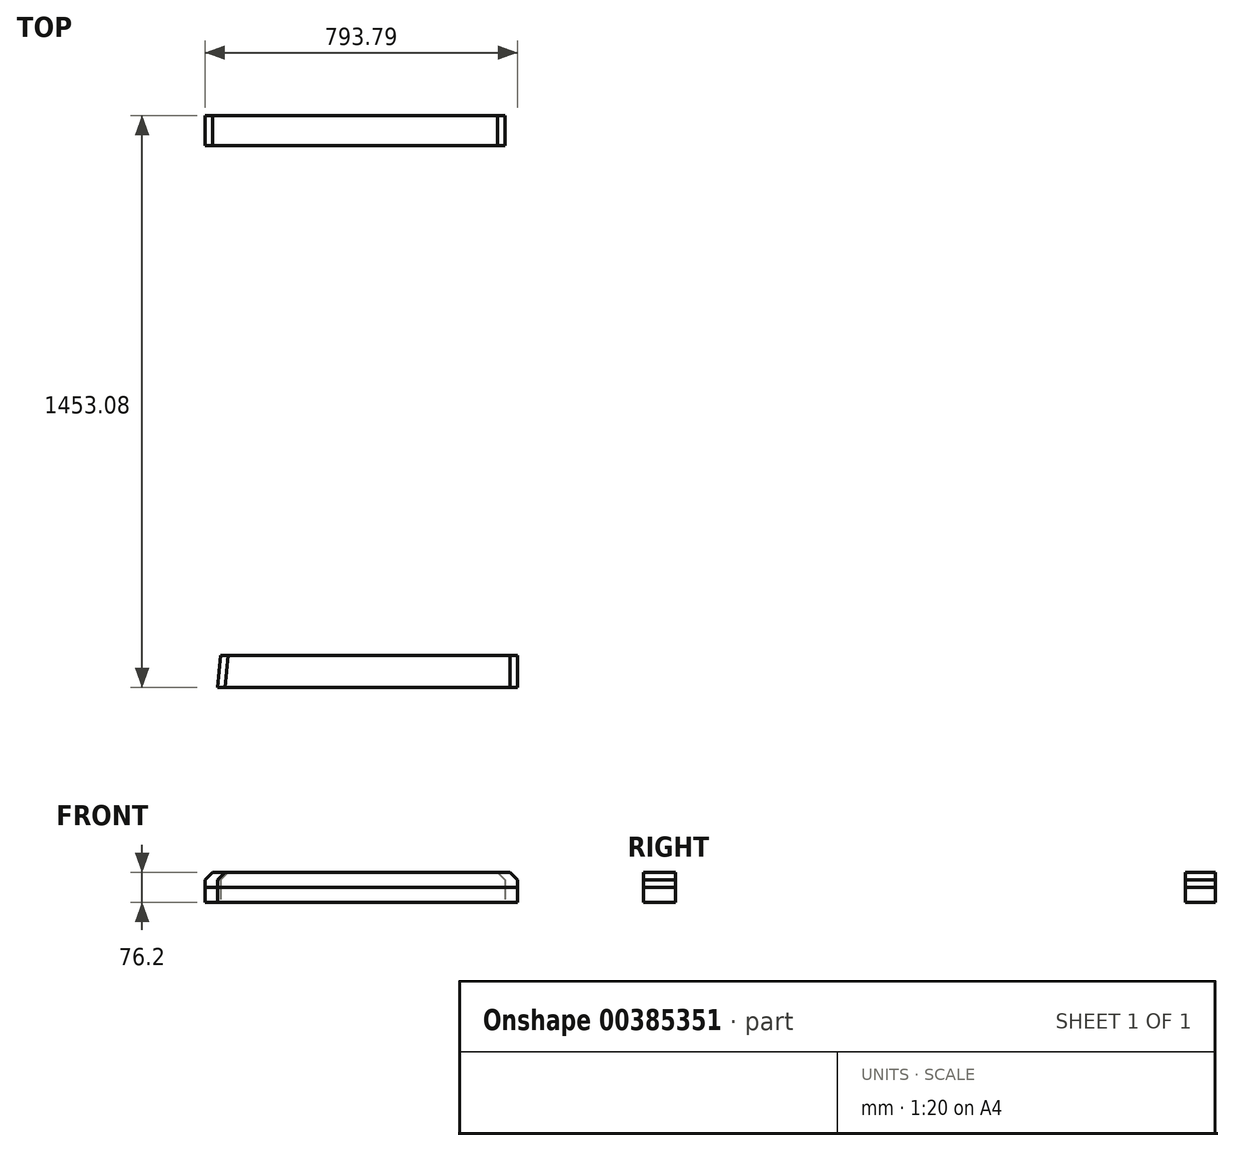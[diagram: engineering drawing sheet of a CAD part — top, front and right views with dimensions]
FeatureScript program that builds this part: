
annotation { "Feature Type Name" : "Feature", "Feature Type Description" : "" }
export const myFeature = defineFeature(function(context is Context, id is Id, definition is map)
    precondition{}
    {
        {
            var Q0;
            Q0=qCreatedBy(makeId("Top.planeOp"),FACE);
            var sketch = newSketch(context, id + "F0", { "sketchPlane" : qUnion([Q0])});
            skLineSegment(sketch, "E0", {"start": v(241.05, 8) * mm, "end": v(241.05, 84.2) * mm});
            skLineSegment(sketch, "E1", {"start": v(241.05, 84.2) * mm, "end": v(1003.05, 84.2) * mm});
            skLineSegment(sketch, "E2", {"start": v(1003.05, 84.2) * mm, "end": v(1003.05, 8) * mm});
            skLineSegment(sketch, "E3", {"start": v(1003.05, 8) * mm, "end": v(241.05, 8) * mm});
            skSolve(sketch);
        }
        {
            var Q0;
            Q0=qCreatedBy(makeId("Top.planeOp"),FACE);
            var sketch = newSketch(context, id + "F1", { "sketchPlane" : qUnion([Q0])});
            skLineSegment(sketch, "E4", {"start": v(280.2, -1287.3) * mm, "end": v(1034.84, -1287.3) * mm});
            skLineSegment(sketch, "E5", {"start": v(1034.84, -1287.3) * mm, "end": v(1034.84, -1368.88) * mm});
            skLineSegment(sketch, "E6", {"start": v(1034.84, -1368.88) * mm, "end": v(272.84, -1368.88) * mm});
            skLineSegment(sketch, "E7", {"start": v(272.84, -1368.88) * mm, "end": v(280.2, -1287.3) * mm});
            skSolve(sketch);
        }
        {
            var Q0;
            Q0=makeQuery(id+"F0.imprint","IMPRINT",FACE,{"disambiguationData":[TD([[makeQuery(id+"F0.imprint","IMPRINT",EDGE,{"derivedFrom":sQuery(id+"F0.wireOp",EDGE,"E0")}),-1.0]])]});
            extrude(context, id + "F2", {"entities" : qUnion([Q0]), "depth" : 38.1 * mm});
        }
        {
            var Q0;
            Q0=makeQuery(id+"F1.imprint","IMPRINT",FACE,{"disambiguationData":[TD([[makeQuery(id+"F1.imprint","IMPRINT",EDGE,{"derivedFrom":sQuery(id+"F1.wireOp",EDGE,"E4")}),-1.0]])]});
            extrude(context, id + "F3", {"entities" : qUnion([Q0]), "depth" : 38.1 * mm});
        }
        {
            var Q0;
            Q0=makeQuery(id+"F2.opExtrude","CAP_FACE",FACE,{"disambiguationData":[OSD([sQuery(id+"F0.wireOp",EDGE,"E0"),sQuery(id+"F0.wireOp",EDGE,"E1"),sQuery(id+"F0.wireOp",EDGE,"E2"),sQuery(id+"F0.wireOp",EDGE,"E3")])],"isStart":false});
            var sketch = newSketch(context, id + "F4", { "sketchPlane" : qUnion([Q0])});
            skLineSegment(sketch, "E8", {"start": v(241.05, 84.2) * mm, "end": v(241.05, 8) * mm});
            skLineSegment(sketch, "E9", {"start": v(241.05, 8) * mm, "end": v(1003.05, 8) * mm});
            skLineSegment(sketch, "E10", {"start": v(1003.05, 8) * mm, "end": v(1003.05, 84.2) * mm});
            skLineSegment(sketch, "E11", {"start": v(1003.05, 84.2) * mm, "end": v(241.05, 84.2) * mm});
            skSolve(sketch);
        }
        {
            var Q0;
            Q0=makeQuery(id+"F4.imprint","IMPRINT",FACE,{"disambiguationData":[TD([[makeQuery(id+"F4.imprint","IMPRINT",EDGE,{"derivedFrom":sQuery(id+"F4.wireOp",EDGE,"E8")}),-1.0]])]});
            extrude(context, id + "F5", {"entities" : qUnion([Q0]), "depth" : 38.1 * mm});
        }
        {
            var Q0;
            Q0=makeQuery(id+"F3.opExtrude","CAP_FACE",FACE,{"disambiguationData":[OSD([sQuery(id+"F1.wireOp",EDGE,"E4"),sQuery(id+"F1.wireOp",EDGE,"E5"),sQuery(id+"F1.wireOp",EDGE,"E6"),sQuery(id+"F1.wireOp",EDGE,"E7")])],"isStart":false});
            var sketch = newSketch(context, id + "F6", { "sketchPlane" : qUnion([Q0])});
            skLineSegment(sketch, "E12", {"start": v(280.2, -1287.3) * mm, "end": v(1034.84, -1287.3) * mm});
            skLineSegment(sketch, "E13", {"start": v(1034.84, -1287.3) * mm, "end": v(1034.84, -1368.88) * mm});
            skLineSegment(sketch, "E14", {"start": v(1034.84, -1368.88) * mm, "end": v(272.84, -1368.88) * mm});
            skLineSegment(sketch, "E15", {"start": v(272.84, -1368.88) * mm, "end": v(280.2, -1287.3) * mm});
            skSolve(sketch);
        }
        {
            var Q0;
            Q0=makeQuery(id+"F6.imprint","IMPRINT",FACE,{"disambiguationData":[TD([[makeQuery(id+"F6.imprint","IMPRINT",EDGE,{"derivedFrom":sQuery(id+"F6.wireOp",EDGE,"E12")}),-1.0]])]});
            extrude(context, id + "F7", {"entities" : qUnion([Q0]), "depth" : 38.1 * mm});
        }
        {
            var Q0;
            Q0=makeQuery(id+"F5.opExtrude","CAP_EDGE",EDGE,{"disambiguationData":[OSD([sQuery(id+"F4.wireOp",EDGE,"E8")])],"isStart":false});
            var Q1;
            Q1=makeQuery(id+"F5.opExtrude","CAP_EDGE",EDGE,{"disambiguationData":[OSD([sQuery(id+"F4.wireOp",EDGE,"E10")])],"isStart":false});
            var Q2;
            Q2=makeQuery(id+"F7.opExtrude","CAP_EDGE",EDGE,{"disambiguationData":[OSD([sQuery(id+"F6.wireOp",EDGE,"E13")])],"isStart":false});
            var Q3;
            Q3=makeQuery(id+"F7.opExtrude","CAP_EDGE",EDGE,{"disambiguationData":[OSD([sQuery(id+"F6.wireOp",EDGE,"E15")])],"isStart":false});
            chamfer(context, id + "F8", {"entities" : qUnion([Q0, Q1, Q2, Q3]), "width" : 19.05 * mm, "tangentPropagation" : true});
        }
    });
